# Revit family: NBS_DudleyIndustriesLimited_PprTwlDpnsrs_PlasmaPaperTowelDispenserSmall
name_source: partatom
category: Furniture
revit_build: Autodesk Revit 2018 (Build: 20190510_1515(x64)
units: mm (PartAtom-declared; Revit-internal decimal feet)

## family parameters
Cut with Voids When Loaded = No
Host = Face
Room Calculation Point = No
Shared = No

## types (1)
- PlasmaPaperTowelDispenserSmall
    AssetType = Fixed
    BIMObjectName = NBS_DudleyIndustriesLimited_PaperTowelDispensers_PlasmaPaperTowelDispenserSmall
    Category = Pr_40_70_22_62:Paper towel dispensers
    Default Elevation = 1050 mm
    Description = Plasma paper towel dispenser
    DispenserMaterial = NBS_DudleyIndustriesLimited_StainlessSteel_Brushed
    DurationUnit = year
    Features = Ideal in locations with restricted space, full seam weld construction
    Finish = Polished/ Brushed/ White Powder Coated
    IfcExportAs = IfcFurnitureType
    IfcExportType = UNDEFINED
    IsBuiltIn = Yes
    ManufacturerName = Dudley Industries Limited
    ManufacturerURL = www.dudleyindustries.com
    Material = Stainless steel
    MaterialsBody = Stainless steel
    MaterialsFinishAndColour = Polished, brushed, white powder coated
    ModelNumber = 78820SS, 78820PS, 78820WH
    ModelReference = PlasmaPaperTowelDispenserSmall
    NBSCertification = www.nationalbimlibrary.com/cert/eatcksk5
    NBSDescription = Paper towel dispensers
    NBSReference = 45-35-72/344
    Name = PaperTowelDispensers_PlasmaPaperTowelDispenserSmall_DudleyIndustriesLimited
    NominalDepth = 124 mm  [stored 0.406824 ft]
    NominalHeight = 211 mm  [stored 0.692257 ft]
    NominalLength = 0 mm  [stored 0 ft]
    NominalWidth = 260 mm  [stored 0.853018 ft]
    ProductInformation = https://www.dudleyindustries.com
    Shape = Rectangular
    Size = 124 x 211 x 260 mm
    Status = UNSET
    Style = Towel dispenser
    TowelsTowelType = C-fold or multi-fold
    Uniclass2015Code = Pr_40_70_22_62
    Uniclass2015Title = Paper towel dispensers
    Uniclass2015Version = Products v1.18
    Version = 1
    WarrantyDescription = 10 Years
    WarrantyDurationUnit = year
    Weight = 1.8 kg

note: [stored X ft] marks values corroborated as IEEE doubles in the binary element streams (Revit-internal decimal feet)

## geometry (parser evidence)
native form markers: Sweep x2
no freeform markers — native parametric forms only
